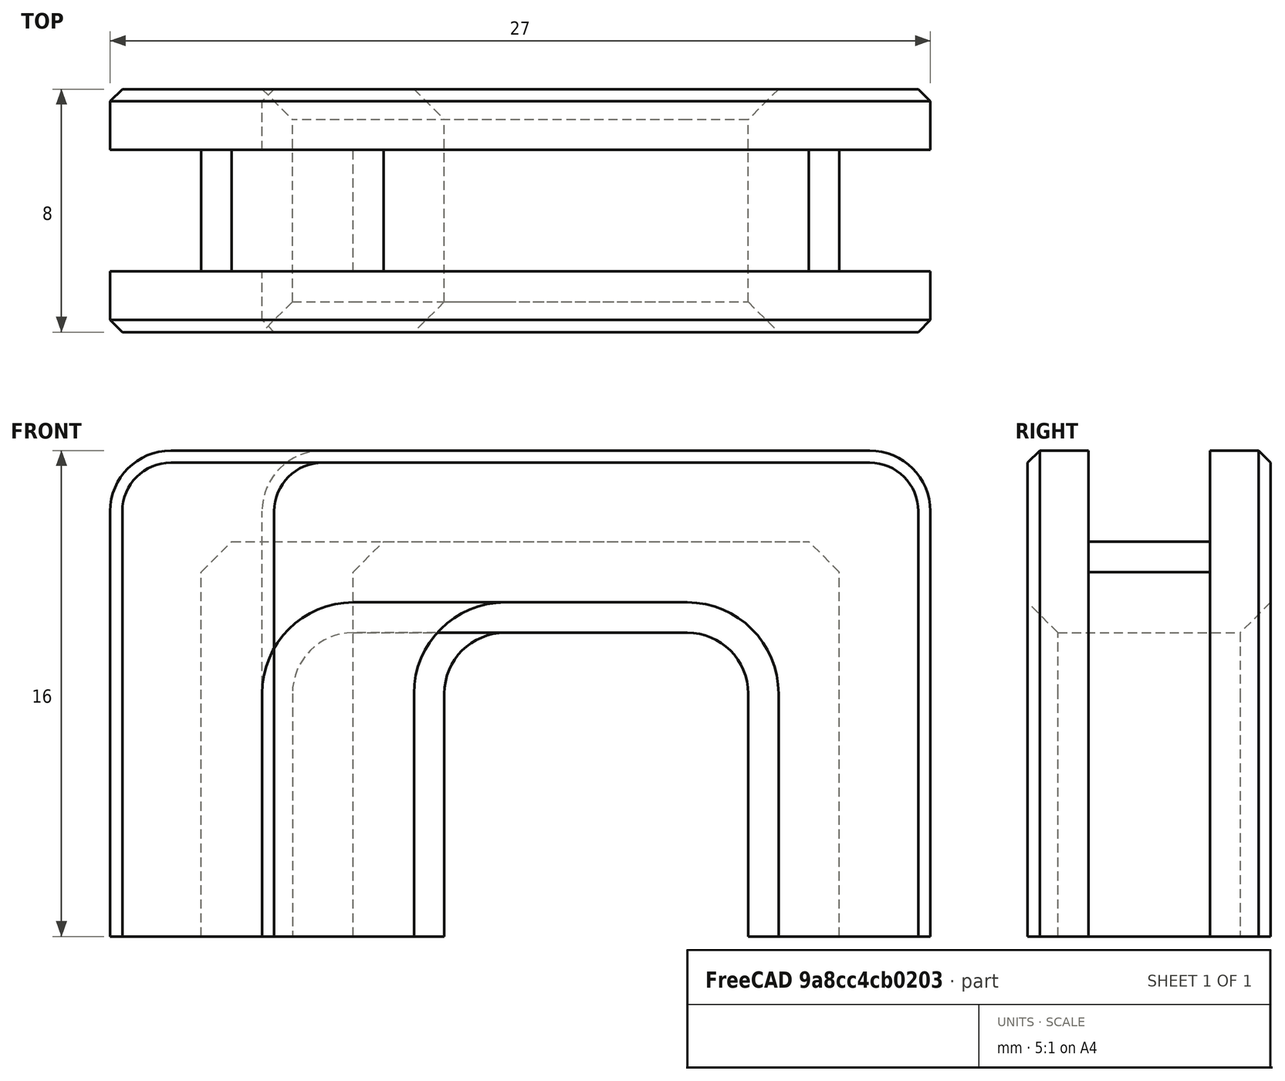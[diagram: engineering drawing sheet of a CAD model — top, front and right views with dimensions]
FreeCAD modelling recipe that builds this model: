
FCSTD DOCUMENT  (FreeCAD 0.19R24291 (Git))
Label: panel-hole
License: Other
LicenseURL: GPL3
objects: Part::Box×7, Part::Feature×4, Part::Cut×3, Part::Chamfer×3, Part::MultiFuse×2, Part::Fillet×2, Part::MultiCommon×1, Part::Refine×1
note: 23 computed .brp shape members not serialized (recipe doc carries the construction recipe); baked Part::Feature solids carry a one-line shape summary decoded from their .brp

FEATURE [Part::Box] Box  label="Cube"
  AttacherType = Attacher::AttachEngine3D
  Height = 19
  Length = 15
  Placement = pos=(-18,2,0) rot=(0,0,1;0rad)
  Width = 4
FEATURE [Part::Box] Box001  label="Cube001"
  AttacherType = Attacher::AttachEngine3D
  Height = 16
  Length = 27
  Placement = pos=(-6,0,0) rot=(0,0,1;0rad)
  Width = 8
FEATURE [Part::Box] Box002  label="Cube002"
  AttacherType = Attacher::AttachEngine3D
  Height = 10
  Length = 15
  Width = 8
FEATURE [Part::Cut] Cut
  Base = -> Box001
  Tool = -> Box002
FEATURE [Part::Box] Box003  label="Cube003"
  AttacherType = Attacher::AttachEngine3D
  Height = 19
  Length = 15
  Placement = pos=(18,2,0) rot=(0,0,1;0rad)
  Width = 4
FEATURE [Part::Box] Box004  label="Cube004"
  AttacherType = Attacher::AttachEngine3D
  Height = 10
  Length = 21
  Placement = pos=(-3,2,13) rot=(0,0,1;0rad)
  Width = 4
FEATURE [Part::MultiFuse] Fusion
  Shapes = -> [Box,Box004,Box003]
FEATURE [Part::Cut] Cut001
  Base = -> Cut
  Tool = -> Fusion
FEATURE [Part::Fillet] Fillet
  Base = -> Cut001
  Edges = 2 edges r=2: [Edge39,Edge44]
FEATURE [Part::Fillet] Fillet001
  Base = -> Fillet
  Edges = 4 edges r=2: [Edge24,Edge31,Edge51,Edge55]
FEATURE [Part::Chamfer] Chamfer
  Base = -> Fillet001
  Edges = 2 edges r=1: [Edge54,Edge70]
FEATURE [Part::Chamfer] Chamfer001
  Base = -> Chamfer
  Edges = 10 edges r=1: [Edge51,Edge52,Edge53,Edge54,Edge55,Edge56,Edge61,Edge62,Edge63,Edge64]
FEATURE [Part::Chamfer] Chamfer002  label="10x15-hole"
  Base = -> Chamfer001
  Edges = 10 edges r=0.4: [Edge17,Edge18,Edge19,Edge20,Edge21,Edge42,Edge43,Edge44,Edge45,Edge46]
FEATURE [Part::Feature] Chamfer002001  label="10x15-hole001"
  shape: bbox 27 x 8 x 16 mm, 50 faces (baked)
FEATURE [Part::Box] Box005  label="Cube005"
  AttacherType = Attacher::AttachEngine3D
  Height = 18
  Length = 19
  Placement = pos=(-11,0,0) rot=(0,0,1;0rad)
  Width = 10
FEATURE [Part::Box] Box006  label="Cube006"
  AttacherType = Attacher::AttachEngine3D
  Height = 18
  Length = 19
  Placement = pos=(-11,0,0) rot=(0,0,1;0rad)
  Width = 10
FEATURE [Part::Feature] Chamfer002002  label="10x15-hole002"
  shape: bbox 27 x 8 x 16 mm, 50 faces (baked)
FEATURE [Part::Cut] Cut002
  Base = -> Chamfer002001
  Tool = -> Box005
FEATURE [Part::MultiCommon] Common
  Placement = pos=(5,0,0) rot=(0,0,1;0rad)
  Shapes = -> [Chamfer002002,Box006]
FEATURE [Part::MultiFuse] Fusion001  label="10x10-hole"
  Shapes = -> [Common,Cut002]
FEATURE [Part::Refine] Fusion001001  label="10x10-hole001"
  Source = -> Fusion001
FEATURE [Part::Feature] Chamfer002003  label="10x15-hole003"
  shape: bbox 27 x 8 x 16 mm, 50 faces (baked)
FEATURE [Part::Feature] Fusion001001001  label="10x10-hole002"
  shape: bbox 22 x 8 x 16 mm, 46 faces (baked)
